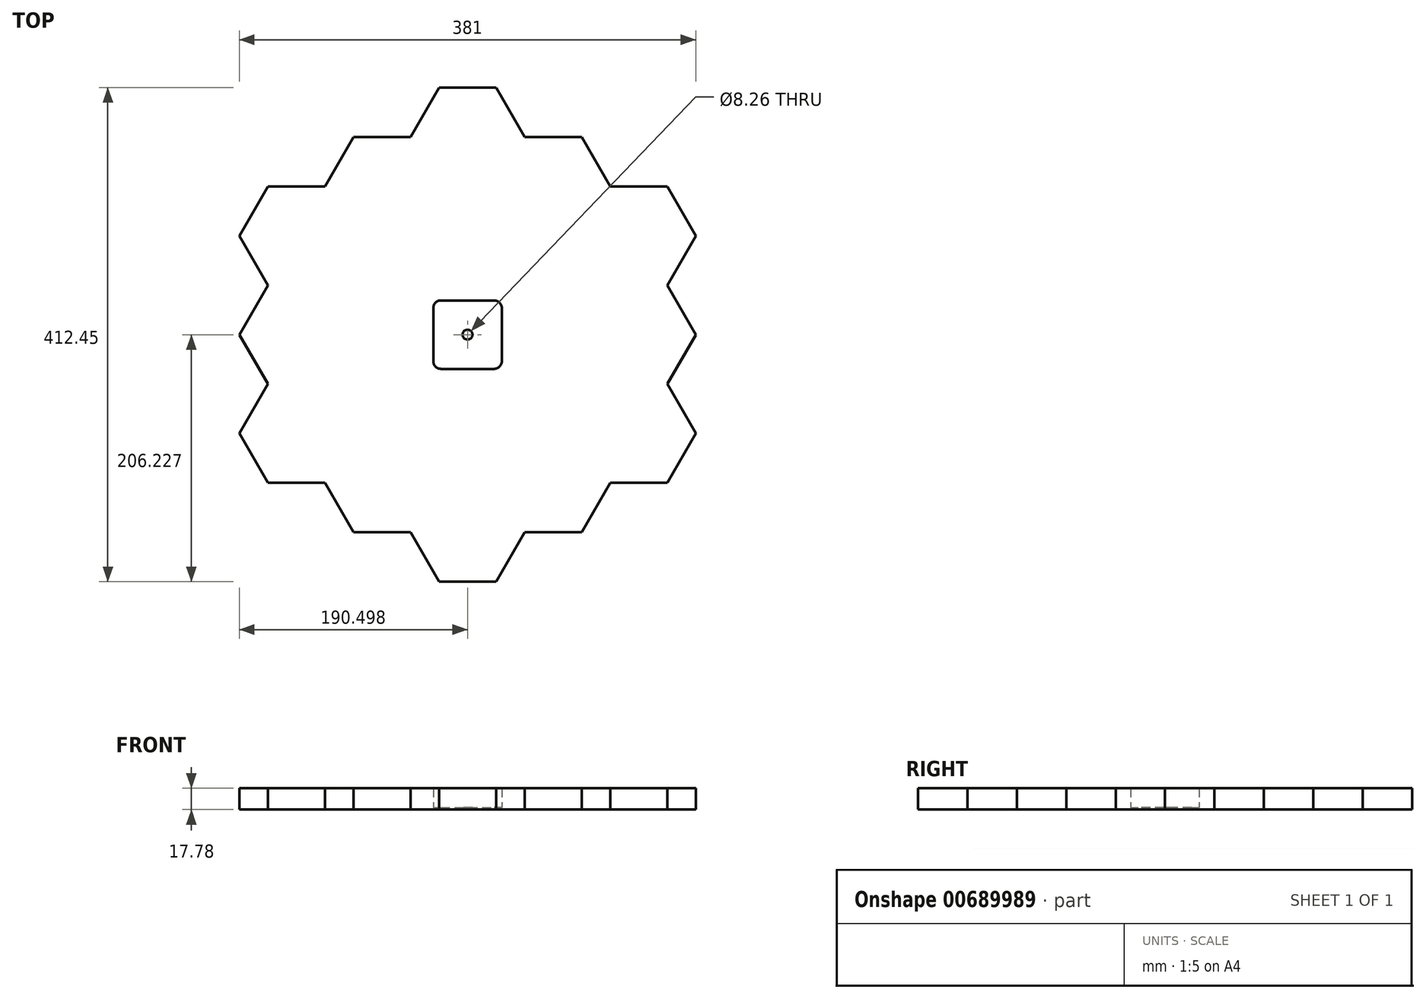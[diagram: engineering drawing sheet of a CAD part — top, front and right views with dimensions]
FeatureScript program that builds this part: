
annotation { "Feature Type Name" : "Feature", "Feature Type Description" : "" }
export const myFeature = defineFeature(function(context is Context, id is Id, definition is map)
    precondition{}
    {
        {
            var Q0;
            Q0=qCreatedBy(makeId("Top.planeOp"),FACE);
            var sketch = newSketch(context, id + "F0", { "sketchPlane" : qUnion([Q0])});
            skCircle(sketch, "E0.cCircle", {"center": v(-81.13, 50.3) * mm, "radius": 40.86 * mm, "construction": true});
            skLineSegment(sketch, "E0.0", {"start": v(-33.95, 50.3) * mm, "end": v(-57.54, 9.43) * mm, "construction": true});
            skLineSegment(sketch, "E0.1", {"start": v(-57.54, 9.43) * mm, "end": v(-104.73, 9.43) * mm, "construction": true});
            skLineSegment(sketch, "E0.2", {"start": v(-104.73, 9.43) * mm, "end": v(-128.32, 50.3) * mm, "construction": true});
            skLineSegment(sketch, "E0.3", {"start": v(-128.32, 50.3) * mm, "end": v(-104.73, 91.16) * mm, "construction": true});
            skLineSegment(sketch, "E0.4", {"start": v(-104.73, 91.16) * mm, "end": v(-57.54, 91.16) * mm, "construction": true});
            skLineSegment(sketch, "E0.5", {"start": v(-57.54, 91.16) * mm, "end": v(-33.95, 50.3) * mm, "construction": true});
            skPoint(sketch, "E0.0.midPoint", {"position": v(-45.74, 29.87) * mm});
            skLineSegment(sketch, "E1.0", {"start": v(-128.76, 50.3) * mm, "end": v(-104.94, 91.54) * mm});
            skLineSegment(sketch, "E1.1", {"start": v(-57.32, 91.54) * mm, "end": v(-33.5, 50.3) * mm});
            skLineSegment(sketch, "E1.2", {"start": v(-33.5, 50.3) * mm, "end": v(-57.32, 9.05) * mm});
            skLineSegment(sketch, "E1.3", {"start": v(-104.94, 91.54) * mm, "end": v(-57.32, 91.54) * mm});
            skLineSegment(sketch, "E1.4", {"start": v(-57.32, 9.05) * mm, "end": v(-104.94, 9.05) * mm});
            skLineSegment(sketch, "E1.5", {"start": v(-104.94, 9.05) * mm, "end": v(-128.76, 50.3) * mm});
            skLineSegment(sketch, "E2.MirrorCS", {"start": v(-33.5, -32.2) * mm, "end": v(-57.32, 9.05) * mm});
            skLineSegment(sketch, "E3.MirrorCS", {"start": v(-57.32, -73.44) * mm, "end": v(-33.5, -32.2) * mm});
            skLineSegment(sketch, "E4.MirrorCS", {"start": v(-104.94, -73.44) * mm, "end": v(-57.32, -73.44) * mm});
            skLineSegment(sketch, "E5.MirrorCS", {"start": v(-128.76, -32.2) * mm, "end": v(-104.94, -73.44) * mm});
            skLineSegment(sketch, "E6.MirrorCS", {"start": v(-104.94, 9.05) * mm, "end": v(-128.76, -32.2) * mm});
            skLineSegment(sketch, "E7.MirrorCS", {"start": v(-128.76, -114.68) * mm, "end": v(-104.94, -73.44) * mm});
            skLineSegment(sketch, "E8.MirrorCS", {"start": v(-104.94, -155.93) * mm, "end": v(-128.76, -114.68) * mm});
            skLineSegment(sketch, "E9.MirrorCS", {"start": v(-57.32, -155.93) * mm, "end": v(-104.94, -155.93) * mm});
            skLineSegment(sketch, "E10.MirrorCS", {"start": v(-33.5, -114.68) * mm, "end": v(-57.32, -155.93) * mm});
            skLineSegment(sketch, "E11.MirrorCS", {"start": v(-57.32, -73.44) * mm, "end": v(-33.5, -114.68) * mm});
            skLineSegment(sketch, "E12.MirrorCS", {"start": v(-128.76, 132.79) * mm, "end": v(-104.94, 91.54) * mm});
            skLineSegment(sketch, "E13.MirrorCS", {"start": v(-104.94, 174.03) * mm, "end": v(-128.76, 132.79) * mm});
            skLineSegment(sketch, "E14.MirrorCS", {"start": v(-57.32, 174.03) * mm, "end": v(-104.94, 174.03) * mm});
            skLineSegment(sketch, "E15.MirrorCS", {"start": v(-33.5, 132.79) * mm, "end": v(-57.32, 174.03) * mm});
            skLineSegment(sketch, "E16.MirrorCS", {"start": v(-57.32, 91.54) * mm, "end": v(-33.5, 132.79) * mm});
            skLineSegment(sketch, "E17.MirrorCS", {"start": v(-104.94, 174.03) * mm, "end": v(-128.76, 215.28) * mm});
            skLineSegment(sketch, "E18.MirrorCS", {"start": v(-128.76, 215.28) * mm, "end": v(-104.94, 256.52) * mm});
            skLineSegment(sketch, "E19.MirrorCS", {"start": v(-33.5, 215.28) * mm, "end": v(-57.32, 174.03) * mm});
            skLineSegment(sketch, "E20.MirrorCS", {"start": v(-57.32, 256.52) * mm, "end": v(-33.5, 215.28) * mm});
            skLineSegment(sketch, "E21.MirrorCS", {"start": v(-104.94, 256.52) * mm, "end": v(-57.32, 256.52) * mm});
            skLineSegment(sketch, "E22.MirrorCS", {"start": v(14.12, 215.28) * mm, "end": v(-33.5, 215.28) * mm});
            skLineSegment(sketch, "E23.MirrorCS", {"start": v(37.93, 174.03) * mm, "end": v(14.12, 215.28) * mm});
            skLineSegment(sketch, "E24.MirrorCS", {"start": v(14.12, 132.79) * mm, "end": v(37.93, 174.03) * mm});
            skLineSegment(sketch, "E25.MirrorCS", {"start": v(-33.5, 132.79) * mm, "end": v(14.12, 132.79) * mm});
            skLineSegment(sketch, "E26.MirrorCS", {"start": v(14.12, 50.3) * mm, "end": v(-33.5, 50.3) * mm});
            skLineSegment(sketch, "E27.MirrorCS", {"start": v(37.93, 91.54) * mm, "end": v(14.12, 50.3) * mm});
            skLineSegment(sketch, "E28.MirrorCS", {"start": v(14.12, 132.79) * mm, "end": v(37.93, 91.54) * mm});
            skLineSegment(sketch, "E29.MirrorCS", {"start": v(37.93, 9.05) * mm, "end": v(14.12, 50.3) * mm});
            skLineSegment(sketch, "E30.MirrorCS", {"start": v(14.12, -32.2) * mm, "end": v(37.93, 9.05) * mm});
            skLineSegment(sketch, "E31.MirrorCS", {"start": v(-33.5, -32.2) * mm, "end": v(14.12, -32.2) * mm});
            skLineSegment(sketch, "E32.MirrorCS", {"start": v(14.12, -114.68) * mm, "end": v(-33.5, -114.68) * mm});
            skLineSegment(sketch, "E33.MirrorCS", {"start": v(37.93, -73.44) * mm, "end": v(14.12, -114.68) * mm});
            skLineSegment(sketch, "E34.MirrorCS", {"start": v(14.12, -32.2) * mm, "end": v(37.93, -73.44) * mm});
            skLineSegment(sketch, "E35", {"start": v(-81.13, 50.3) * mm, "end": v(-81.13, 91.16) * mm, "construction": true});
            skLineSegment(sketch, "E36", {"start": v(-81.13, 50.3) * mm, "end": v(-40.27, 50.3) * mm, "construction": true});
            skLineSegment(sketch, "E37", {"start": v(-9.7, 132.79) * mm, "end": v(-9.7, 50.3) * mm, "construction": true});
            skLineSegment(sketch, "E38.MirrorCS", {"start": v(85.56, -73.44) * mm, "end": v(37.93, -73.44) * mm});
            skLineSegment(sketch, "E39.MirrorCS", {"start": v(109.37, -32.2) * mm, "end": v(85.56, -73.44) * mm});
            skLineSegment(sketch, "E40.MirrorCS", {"start": v(85.56, 9.05) * mm, "end": v(109.37, -32.2) * mm});
            skLineSegment(sketch, "E41.MirrorCS", {"start": v(37.93, 9.05) * mm, "end": v(85.56, 9.05) * mm});
            skLineSegment(sketch, "E42.MirrorCS", {"start": v(85.56, 9.05) * mm, "end": v(109.37, 50.3) * mm});
            skLineSegment(sketch, "E43.MirrorCS", {"start": v(109.37, 50.3) * mm, "end": v(85.56, 91.54) * mm});
            skLineSegment(sketch, "E44.MirrorCS", {"start": v(85.56, 91.54) * mm, "end": v(37.93, 91.54) * mm});
            skLineSegment(sketch, "E45.MirrorCS", {"start": v(37.93, 174.03) * mm, "end": v(85.56, 174.03) * mm});
            skLineSegment(sketch, "E46.MirrorCS", {"start": v(109.37, 132.79) * mm, "end": v(85.56, 91.54) * mm});
            skLineSegment(sketch, "E47.MirrorCS", {"start": v(85.56, 174.03) * mm, "end": v(109.37, 132.79) * mm});
            skLineSegment(sketch, "E48.MirrorCS", {"start": v(-200.2, 174.03) * mm, "end": v(-176.38, 215.28) * mm});
            skLineSegment(sketch, "E49.MirrorCS", {"start": v(-271.63, -32.2) * mm, "end": v(-247.82, -73.44) * mm});
            skLineSegment(sketch, "E50.MirrorCS", {"start": v(-200.2, 91.54) * mm, "end": v(-176.38, 50.3) * mm});
            skLineSegment(sketch, "E51.MirrorCS", {"start": v(-271.63, 50.3) * mm, "end": v(-247.82, 91.54) * mm});
            skLineSegment(sketch, "E52.MirrorCS", {"start": v(-176.38, -32.2) * mm, "end": v(-200.2, 9.05) * mm});
            skLineSegment(sketch, "E53.MirrorCS", {"start": v(-271.63, 132.79) * mm, "end": v(-247.82, 91.54) * mm});
            skLineSegment(sketch, "E54.MirrorCS", {"start": v(-176.38, 215.28) * mm, "end": v(-128.76, 215.28) * mm});
            skLineSegment(sketch, "E55.MirrorCS", {"start": v(-247.82, -73.44) * mm, "end": v(-200.2, -73.44) * mm});
            skLineSegment(sketch, "E56.MirrorCS", {"start": v(-176.38, 50.3) * mm, "end": v(-128.76, 50.3) * mm});
            skLineSegment(sketch, "E57.MirrorCS", {"start": v(-128.76, -32.2) * mm, "end": v(-176.38, -32.2) * mm});
            skLineSegment(sketch, "E58.MirrorCS", {"start": v(-247.82, 174.03) * mm, "end": v(-271.63, 132.79) * mm});
            skLineSegment(sketch, "E59.MirrorCS", {"start": v(-247.82, 9.05) * mm, "end": v(-271.63, 50.3) * mm});
            skLineSegment(sketch, "E60.MirrorCS", {"start": v(-200.2, 174.03) * mm, "end": v(-247.82, 174.03) * mm});
            skLineSegment(sketch, "E61.MirrorCS", {"start": v(-200.2, 9.05) * mm, "end": v(-176.38, 50.3) * mm});
            skLineSegment(sketch, "E62.MirrorCS", {"start": v(-200.2, -73.44) * mm, "end": v(-176.38, -114.68) * mm});
            skLineSegment(sketch, "E63.MirrorCS", {"start": v(-152.57, 132.79) * mm, "end": v(-152.57, 50.3) * mm, "construction": true});
            skLineSegment(sketch, "E64.MirrorCS", {"start": v(-176.38, 132.79) * mm, "end": v(-200.2, 91.54) * mm});
            skLineSegment(sketch, "E65.MirrorCS", {"start": v(-247.82, 9.05) * mm, "end": v(-271.63, -32.2) * mm});
            skLineSegment(sketch, "E66.MirrorCS", {"start": v(-176.38, -114.68) * mm, "end": v(-128.76, -114.68) * mm});
            skLineSegment(sketch, "E67.MirrorCS", {"start": v(-247.82, 91.54) * mm, "end": v(-200.2, 91.54) * mm});
            skLineSegment(sketch, "E68.MirrorCS", {"start": v(-176.38, 132.79) * mm, "end": v(-200.2, 174.03) * mm});
            skLineSegment(sketch, "E69.MirrorCS", {"start": v(-128.76, 132.79) * mm, "end": v(-176.38, 132.79) * mm});
            skLineSegment(sketch, "E70.MirrorCS", {"start": v(-200.2, 9.05) * mm, "end": v(-247.82, 9.05) * mm});
            skLineSegment(sketch, "E71.MirrorCS", {"start": v(-176.38, -32.2) * mm, "end": v(-200.2, -73.44) * mm});
            skPoint(sketch, "E72.MirrorP", {"position": v(-116.52, 29.87) * mm});
            skCircle(sketch, "E73", {"center": v(-81.13, 50.3) * mm, "radius": 4.13 * mm});
            skSolve(sketch);
        }
        {
            var Q0;
            Q0=qCreatedBy(makeId("Top.planeOp"),FACE);
            var sketch = newSketch(context, id + "F1", { "sketchPlane" : qUnion([Q0])});
            skLineSegment(sketch, "E74.0", {"start": v(-247.82, 9.05) * mm, "end": v(-271.63, -32.2) * mm});
            skLineSegment(sketch, "E74.1", {"start": v(-271.63, -32.2) * mm, "end": v(-247.82, -73.44) * mm});
            skLineSegment(sketch, "E74.2", {"start": v(-247.82, -73.44) * mm, "end": v(-200.2, -73.44) * mm});
            skLineSegment(sketch, "E74.3", {"start": v(-247.82, 9.05) * mm, "end": v(-271.63, 50.3) * mm});
            skLineSegment(sketch, "E74.4", {"start": v(-271.63, 50.3) * mm, "end": v(-247.82, 91.54) * mm});
            skLineSegment(sketch, "E74.5", {"start": v(-271.63, 132.79) * mm, "end": v(-247.82, 91.54) * mm});
            skLineSegment(sketch, "E74.6", {"start": v(-247.82, 174.03) * mm, "end": v(-271.63, 132.79) * mm});
            skLineSegment(sketch, "E74.7", {"start": v(-200.2, 174.03) * mm, "end": v(-247.82, 174.03) * mm});
            skLineSegment(sketch, "E74.8", {"start": v(-200.2, 174.03) * mm, "end": v(-176.38, 215.28) * mm});
            skLineSegment(sketch, "E74.9", {"start": v(-176.38, 215.28) * mm, "end": v(-128.76, 215.28) * mm});
            skLineSegment(sketch, "E74.10", {"start": v(-128.76, 215.28) * mm, "end": v(-104.94, 256.52) * mm});
            skLineSegment(sketch, "E74.11", {"start": v(-104.94, 256.52) * mm, "end": v(-57.32, 256.52) * mm});
            skLineSegment(sketch, "E74.12", {"start": v(-57.32, 256.52) * mm, "end": v(-33.5, 215.28) * mm});
            skLineSegment(sketch, "E74.13", {"start": v(14.12, 215.28) * mm, "end": v(-33.5, 215.28) * mm});
            skLineSegment(sketch, "E74.14", {"start": v(37.93, 174.03) * mm, "end": v(14.12, 215.28) * mm});
            skLineSegment(sketch, "E74.15", {"start": v(37.93, 174.03) * mm, "end": v(85.56, 174.03) * mm});
            skLineSegment(sketch, "E74.16", {"start": v(85.56, 174.03) * mm, "end": v(109.37, 132.79) * mm});
            skLineSegment(sketch, "E74.17", {"start": v(109.37, 132.79) * mm, "end": v(85.56, 91.54) * mm});
            skLineSegment(sketch, "E74.18", {"start": v(109.37, 50.3) * mm, "end": v(85.56, 91.54) * mm});
            skLineSegment(sketch, "E74.19", {"start": v(85.56, 9.05) * mm, "end": v(109.37, 50.3) * mm});
            skLineSegment(sketch, "E74.20", {"start": v(85.56, 9.05) * mm, "end": v(109.37, -32.2) * mm});
            skLineSegment(sketch, "E74.21", {"start": v(109.37, -32.2) * mm, "end": v(85.56, -73.44) * mm});
            skLineSegment(sketch, "E74.22", {"start": v(85.56, -73.44) * mm, "end": v(37.93, -73.44) * mm});
            skLineSegment(sketch, "E74.23", {"start": v(37.93, -73.44) * mm, "end": v(14.12, -114.68) * mm});
            skLineSegment(sketch, "E74.24", {"start": v(14.12, -114.68) * mm, "end": v(-33.5, -114.68) * mm});
            skLineSegment(sketch, "E74.25", {"start": v(-33.5, -114.68) * mm, "end": v(-57.32, -155.93) * mm});
            skLineSegment(sketch, "E74.26", {"start": v(-57.32, -155.93) * mm, "end": v(-104.94, -155.93) * mm});
            skLineSegment(sketch, "E74.27", {"start": v(-104.94, -155.93) * mm, "end": v(-128.76, -114.68) * mm});
            skLineSegment(sketch, "E74.28", {"start": v(-176.38, -114.68) * mm, "end": v(-128.76, -114.68) * mm});
            skLineSegment(sketch, "E74.29", {"start": v(-200.2, -73.44) * mm, "end": v(-176.38, -114.68) * mm});
            skLineSegment(sketch, "E75.bottom", {"start": v(-103.36, 78.87) * mm, "end": v(-58.9, 78.87) * mm});
            skLineSegment(sketch, "E75.top", {"start": v(-103.36, 21.72) * mm, "end": v(-58.9, 21.72) * mm});
            skLineSegment(sketch, "E75.left", {"start": v(-109.7, 72.52) * mm, "end": v(-109.7, 28.07) * mm});
            skLineSegment(sketch, "E75.right", {"start": v(-52.56, 72.52) * mm, "end": v(-52.56, 28.07) * mm});
            skPoint(sketch, "E76", {"position": v(-52.56, 50.3) * mm});
            skPoint(sketch, "E77", {"position": v(-81.13, 21.72) * mm});
            skCircle(sketch, "E78", {"center": v(-81.13, 50.3) * mm, "radius": 4.13 * mm});
            skPoint(sketch, "E79.visualSharp", {"position": v(-109.7, 78.87) * mm});
            skArc(sketch, "E79.filletArc", {"start": v(-103.36, 78.87) * mm, "mid": v(-107.85, 77.01) * mm, "end": v(-109.7, 72.52) * mm});
            skPoint(sketch, "E80.visualSharp", {"position": v(-52.56, 78.87) * mm});
            skArc(sketch, "E80.filletArc", {"start": v(-52.56, 72.52) * mm, "mid": v(-54.42, 77.01) * mm, "end": v(-58.9, 78.87) * mm});
            skPoint(sketch, "E81.visualSharp", {"position": v(-52.56, 21.72) * mm});
            skArc(sketch, "E81.filletArc", {"start": v(-58.9, 21.72) * mm, "mid": v(-54.42, 23.58) * mm, "end": v(-52.56, 28.07) * mm});
            skPoint(sketch, "E82.visualSharp", {"position": v(-109.7, 21.72) * mm});
            skArc(sketch, "E82.filletArc", {"start": v(-109.7, 28.07) * mm, "mid": v(-107.85, 23.58) * mm, "end": v(-103.36, 21.72) * mm});
            skSolve(sketch);
        }
        {
            var Q0;
            Q0=makeQuery(id+"F1.imprint","IMPRINT",FACE,{"disambiguationData":[TD([[makeQuery(id+"F1.imprint","IMPRINT",EDGE,{"derivedFrom":sQuery(id+"F1.wireOp",EDGE,"E74.0")}),1.0]])]});
            extrude(context, id + "F2", {"entities" : qUnion([Q0]), "depth" : 17.78 * mm, "offsetDistance" : 25.4 * mm});
        }
        {
            var Q0;
            Q0=makeQuery(id+"F1.imprint","IMPRINT",FACE,{"disambiguationData":[TD([[makeQuery(id+"F1.imprint","IMPRINT",EDGE,{"derivedFrom":sQuery(id+"F1.wireOp",EDGE,"E75.bottom")}),-1.0]])]});
            extrude(context, id + "F3", {"entities" : qUnion([Q0]), "operationType" : NewBodyOperationType.ADD, "depth" : 1.71 * mm, "offsetDistance" : 25.4 * mm});
        }
    });
